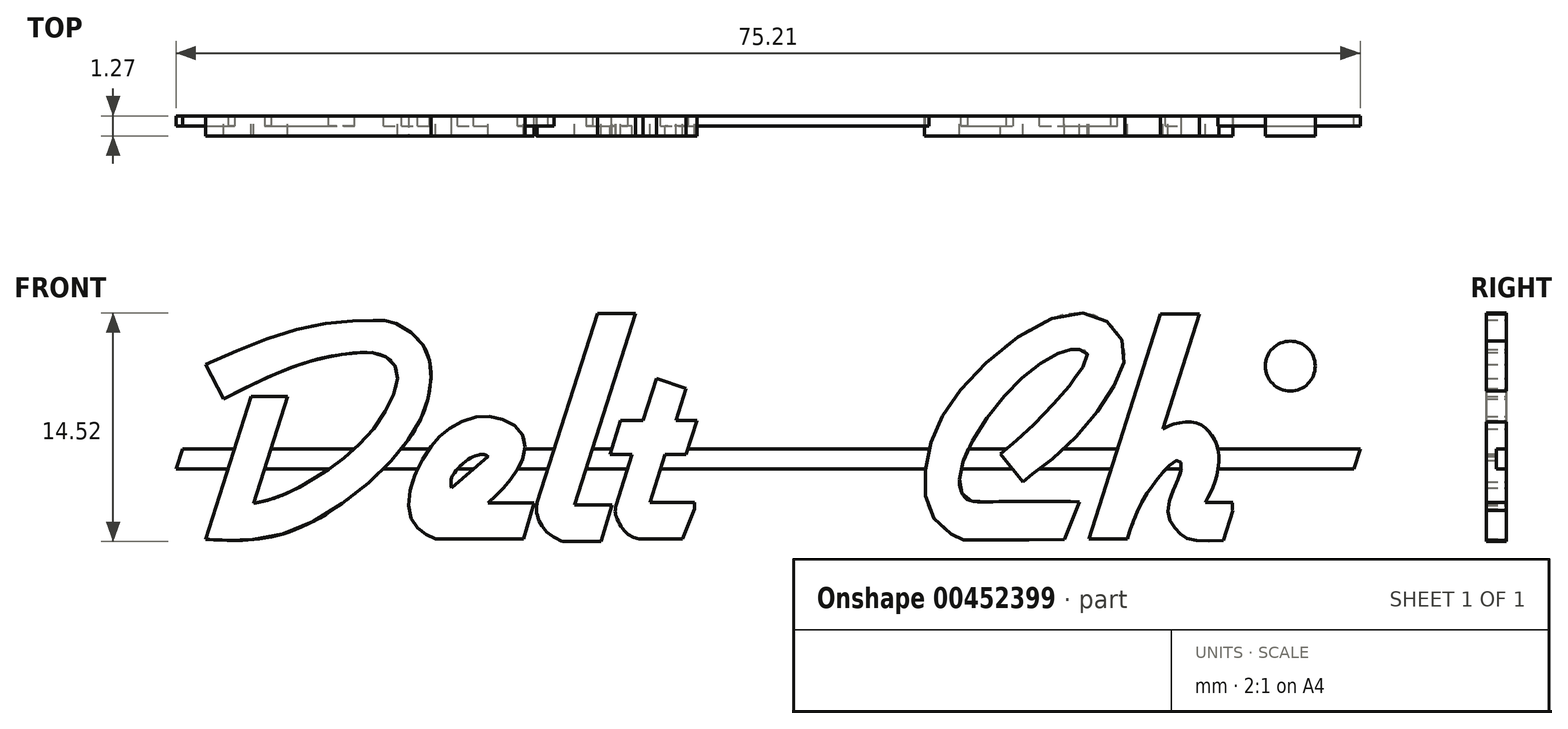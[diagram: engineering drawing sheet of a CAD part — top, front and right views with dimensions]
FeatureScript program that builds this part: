
annotation { "Feature Type Name" : "Feature", "Feature Type Description" : "" }
export const myFeature = defineFeature(function(context is Context, id is Id, definition is map)
    precondition{}
    {
        {
            var Q0;
            Q0=qCreatedBy(makeId("Front.planeOp"),FACE);
            var sketch = newSketch(context, id + "F0", { "sketchPlane" : qUnion([Q0])});
            skCircle(sketch, "E0", {"center": v(0, 0) * mm, "radius": 1.59 * mm});
            skCircle(sketch, "E1", {"center": v(82.55, 0) * mm, "radius": 1.59 * mm});
            skLineSegment(sketch, "E2", {"start": v(0, 0) * mm, "end": v(82.55, 0) * mm, "construction": true});
            skLineSegment(sketch, "E3", {"start": v(-6.39, 0) * mm, "end": v(88.9, 0) * mm, "construction": true});
            skEllipticalArc(sketch, "E4", {});
            skLineSegment(sketch, "E5", {"start": v(9.24, 2.96) * mm, "end": v(6.34, -6.11) * mm});
            skFitSpline(sketch, "E6", {"points": [v(6.34, -6.11) * mm, v(11.08, -5.82) * mm, v(17.7, -1.6) * mm, v(20.28, 2.23) * mm, v(20.6, 5.05) * mm, v(19.68, 6.78) * mm, v(17.97, 7.76) * mm, v(17.26, 7.8) * mm, v(13.33, 7.5) * mm, v(6.34, 4.98) * mm], "startDerivative": vector(26.1, -1) * mm, "endDerivative": vector(-45.15, -19.97) * mm});
            skLineSegment(sketch, "E7", {"start": v(9.24, 2.96) * mm, "end": v(11.56, 2.96) * mm});
            skLineSegment(sketch, "E8", {"start": v(11.56, 2.96) * mm, "end": v(9.38, -3.85) * mm});
            skFitSpline(sketch, "E9", {"points": [v(7.49, 2.8) * mm, v(9.85, 3.98) * mm, v(13.03, 5.22) * mm, v(15.23, 5.65) * mm, v(17.24, 5.7) * mm, v(18.43, 4.83) * mm, v(18.24, 2.96) * mm, v(16.2, 0) * mm, v(13.6, -2) * mm, v(11.58, -3.15) * mm, v(9.38, -3.85) * mm], "startDerivative": vector(21.38, 11.17) * mm, "endDerivative": vector(-26.6, -5.77) * mm});
            skLineSegment(sketch, "E10", {"start": v(6.34, 4.98) * mm, "end": v(7.49, 2.8) * mm});
            skLineSegment(sketch, "E11", {"start": v(24.28, -3.78) * mm, "end": v(27.21, -3.78) * mm});
            skLineSegment(sketch, "E12", {"start": v(27.21, -3.78) * mm, "end": v(26.52, -6.1) * mm});
            skLineSegment(sketch, "E13", {"start": v(26.52, -6.1) * mm, "end": v(20.93, -6.1) * mm});
            skFitSpline(sketch, "E14", {"points": [v(20.93, -6.1) * mm, v(20.03, -5.59) * mm, v(19.32, -4.54) * mm, v(19.49, -2.43) * mm, v(20.67, -0.21) * mm, v(21.8, 0.91) * mm, v(23.6, 1.67) * mm, v(25.31, 1.46) * mm, v(26.5, 0.48) * mm, v(26.5, -0.97) * mm, v(25.82, -2.13) * mm, v(25.09, -3.03) * mm, v(24.28, -3.78) * mm], "startDerivative": vector(-13.64, 6.23) * mm, "endDerivative": vector(-11.8, -10.28) * mm});
            skFitSpline(sketch, "E15", {"points": [v(21.97, -2.84) * mm, v(24.28, -0.85) * mm], "startDerivative": vector(2.31, 2) * mm, "endDerivative": vector(2.31, 2) * mm});
            skFitSpline(sketch, "E16", {"points": [v(21.97, -2.84) * mm, v(21.97, -2.19) * mm, v(22.96, -1.08) * mm, v(23.77, -0.73) * mm, v(24.28, -0.85) * mm], "startDerivative": vector(-0.63, 2.9) * mm, "endDerivative": vector(2.1, -1.88) * mm});
            skLineSegment(sketch, "E17", {"start": v(33.65, 8.22) * mm, "end": v(29.76, -3.94) * mm});
            skLineSegment(sketch, "E18", {"start": v(31.22, 8.22) * mm, "end": v(27.4, -3.75) * mm});
            skFitSpline(sketch, "E19", {"points": [v(27.4, -3.75) * mm, v(27.35, -4.28) * mm, v(27.67, -5.21) * mm, v(28.18, -5.78) * mm, v(28.68, -6.1) * mm, v(29.16, -6.25) * mm], "startDerivative": vector(-0.56, -2.65) * mm, "endDerivative": vector(2.82, 0.02) * mm});
            skLineSegment(sketch, "E20", {"start": v(29.16, -6.25) * mm, "end": v(31.45, -6.25) * mm});
            skLineSegment(sketch, "E21", {"start": v(31.45, -6.25) * mm, "end": v(32.16, -3.94) * mm});
            skLineSegment(sketch, "E22", {"start": v(32.16, -3.94) * mm, "end": v(29.76, -3.94) * mm});
            skLineSegment(sketch, "E23", {"start": v(33.65, 8.22) * mm, "end": v(31.22, 8.22) * mm});
            skLineSegment(sketch, "E24", {"start": v(32.7, 1.44) * mm, "end": v(34.12, 1.44) * mm});
            skLineSegment(sketch, "E25", {"start": v(37.55, 1.44) * mm, "end": v(36.86, -0.72) * mm});
            skLineSegment(sketch, "E26", {"start": v(36.86, -0.72) * mm, "end": v(35.52, -0.72) * mm});
            skLineSegment(sketch, "E27", {"start": v(32, -0.72) * mm, "end": v(32.7, 1.44) * mm});
            skLineSegment(sketch, "E28", {"start": v(34.97, 4.1) * mm, "end": v(34.12, 1.44) * mm});
            skFitSpline(sketch, "E29", {"points": [v(32.39, -3.97) * mm, v(32.39, -4.56) * mm, v(32.96, -5.6) * mm, v(33.66, -6.04) * mm, v(34.2, -6.08) * mm], "startDerivative": vector(-0.48, -3.27) * mm, "endDerivative": vector(2.58, 0) * mm});
            skLineSegment(sketch, "E30", {"start": v(34.2, -6.08) * mm, "end": v(36.64, -6.08) * mm});
            skLineSegment(sketch, "E31", {"start": v(36.64, -6.08) * mm, "end": v(37.38, -4.18) * mm});
            skLineSegment(sketch, "E32", {"start": v(37.4, -3.76) * mm, "end": v(34.55, -3.76) * mm});
            skLineSegment(sketch, "E33", {"start": v(34.55, -3.76) * mm, "end": v(35.52, -0.72) * mm});
            skLineSegment(sketch, "E34", {"start": v(36.86, 3.48) * mm, "end": v(34.97, 4.1) * mm});
            skLineSegment(sketch, "E35.trimOffspring", {"start": v(33.43, -0.72) * mm, "end": v(32.39, -3.97) * mm});
            skLineSegment(sketch, "E36.trimOffspring", {"start": v(36.21, 1.44) * mm, "end": v(36.86, 3.48) * mm});
            skLineSegment(sketch, "E37.trimOffspring", {"start": v(36.21, 1.44) * mm, "end": v(37.55, 1.44) * mm});
            skLineSegment(sketch, "E38.trimOffspring", {"start": v(33.43, -0.72) * mm, "end": v(32, -0.72) * mm});
            skFitSpline(sketch, "E39", {"points": [v(44.77, 1.43) * mm, v(41.69, 1) * mm, v(39.37, -0.26) * mm, v(37.87, -1.95) * mm, v(37.42, -3.48) * mm, v(37.55, -4.94) * mm, v(38.8, -6.04) * mm, v(40.81, -6.23) * mm, v(41.86, -5.63) * mm], "startDerivative": vector(-20.32, -1.3) * mm, "endDerivative": vector(9.3, 7.4) * mm});
            skFitSpline(sketch, "E40", {"points": [v(44.9, -0.76) * mm, v(44.25, -0.77) * mm, v(43.6, -0.86) * mm, v(41.6, -1.5) * mm, v(40.12, -2.55) * mm, v(39.68, -3.26) * mm, v(39.72, -3.97) * mm, v(40.65, -4) * mm, v(41.84, -2.63) * mm, v(42.1, -1.54) * mm], "startDerivative": vector(-16.55, 0.4) * mm, "endDerivative": vector(1.05, 9.2) * mm});
            skLineSegment(sketch, "E41", {"start": v(41.86, -5.63) * mm, "end": v(42.25, -5.63) * mm});
            skFitSpline(sketch, "E42", {"points": [v(42.25, -5.63) * mm, v(42.32, -5.88) * mm, v(42.53, -6.08) * mm, v(42.85, -6.13) * mm, v(42.86, -6.13) * mm], "startDerivative": vector(0.14, -0.88) * mm, "endDerivative": vector(0.11, 0.01) * mm});
            skLineSegment(sketch, "E43", {"start": v(42.85, -6.13) * mm, "end": v(45.2, -6.13) * mm});
            skLineSegment(sketch, "E44", {"start": v(45.2, -6.13) * mm, "end": v(46.1, -3.87) * mm});
            skLineSegment(sketch, "E45", {"start": v(46.1, -3.87) * mm, "end": v(43.54, -3.87) * mm});
            skFitSpline(sketch, "E46", {"points": [v(43.54, -3.87) * mm, v(43.87, -3.3) * mm, v(44.12, -2.21) * mm], "startDerivative": vector(0.7, 0.97) * mm, "endDerivative": vector(0.42, 3.16) * mm});
            skLineSegment(sketch, "E47", {"start": v(42.1, -1.54) * mm, "end": v(44.12, -2.21) * mm});
            skPoint(sketch, "E48.orphan", {"position": v(37.55, -3.76) * mm});
            skFitSpline(sketch, "E49", {"points": [v(56.83, -0.67) * mm, v(59.11, 1.35) * mm, v(61.4, 3.9) * mm, v(61.53, 4.1) * mm, v(62.26, 5.2) * mm, v(62.24, 5.84) * mm, v(61.58, 5.94) * mm, v(61.21, 5.94) * mm, v(59.63, 5.22) * mm, v(57, 2.92) * mm, v(54.62, -0.7) * mm, v(54.23, -2.62) * mm, v(54.65, -3.53) * mm, v(56.23, -3.72) * mm, v(61.83, -3.72) * mm], "startDerivative": vector(22.62, 18.51) * mm, "endDerivative": vector(50.2, -0.32) * mm});
            skFitSpline(sketch, "E50", {"points": [v(58.25, -2.47) * mm, v(58.7, -2.1) * mm, v(60.92, -0.33) * mm, v(63.78, 3.2) * mm, v(64.72, 5.72) * mm, v(63.66, 7.68) * mm, v(60.58, 8.1) * mm, v(55.2, 4.4) * mm, v(52.68, 0.8) * mm, v(52, -2.47) * mm, v(52.65, -4.84) * mm, v(54.17, -6.04) * mm, v(54.5, -6.14) * mm, v(54.66, -6.14) * mm, v(60.94, -6.13) * mm, v(60.95, -6.13) * mm], "startDerivative": vector(19.14, 15.4) * mm, "endDerivative": vector(-1.69, 2.05) * mm});
            skLineSegment(sketch, "E51", {"start": v(60.89, -6.13) * mm, "end": v(61.83, -3.72) * mm});
            skLineSegment(sketch, "E52", {"start": v(56.83, -0.67) * mm, "end": v(58.25, -2.47) * mm});
            skLineSegment(sketch, "E53", {"start": v(62.43, -6.08) * mm, "end": v(67, 8.2) * mm});
            skLineSegment(sketch, "E54", {"start": v(67, 8.2) * mm, "end": v(69.47, 8.2) * mm});
            skLineSegment(sketch, "E55", {"start": v(69.47, 8.2) * mm, "end": v(67.13, 0.89) * mm});
            skLineSegment(sketch, "E56", {"start": v(62.43, -6.08) * mm, "end": v(64.87, -6.08) * mm});
            skFitSpline(sketch, "E57", {"points": [v(64.87, -6.08) * mm, v(65.31, -4.84) * mm, v(65.94, -3.47) * mm, v(66.66, -2.46) * mm, v(67.33, -1.62) * mm, v(68.12, -1.1) * mm, v(68.32, -1.56) * mm, v(67.8, -3.01) * mm, v(67.5, -4.64) * mm, v(68.03, -5.54) * mm, v(68.78, -6.08) * mm, v(70.97, -6.18) * mm], "startDerivative": vector(3.34, 11.27) * mm, "endDerivative": vector(21.52, 0.39) * mm});
            skLineSegment(sketch, "E58", {"start": v(71.57, -4.3) * mm, "end": v(70.97, -6.18) * mm});
            skFitSpline(sketch, "E59", {"points": [v(67.13, 0.89) * mm, v(67.84, 1.2) * mm, v(69.29, 1.28) * mm, v(70.15, 0.6) * mm, v(70.66, -0.47) * mm, v(70.45, -2.45) * mm, v(69.83, -3.76) * mm], "startDerivative": vector(4.73, 2.62) * mm, "endDerivative": vector(-3.74, -6.76) * mm});
            skLineSegment(sketch, "E60", {"start": v(69.83, -3.76) * mm, "end": v(71.57, -3.76) * mm});
            skLineSegment(sketch, "E61", {"start": v(77.73, 8.35) * mm, "end": v(77.71, 8.29) * mm});
            skLineSegment(sketch, "E62", {"start": v(73.22, 1.43) * mm, "end": v(71.58, -3.72) * mm});
            skFitSpline(sketch, "E63", {"points": [v(71.58, -3.72) * mm, v(71.56, -4.21) * mm, v(71.88, -5.15) * mm, v(72.4, -5.72) * mm, v(72.9, -6.03) * mm, v(73.34, -6.22) * mm], "startDerivative": vector(-0.56, -2.65) * mm, "endDerivative": vector(2.82, 0.02) * mm});
            skLineSegment(sketch, "E64", {"start": v(73.34, -6.22) * mm, "end": v(75.37, -6.22) * mm});
            skLineSegment(sketch, "E65", {"start": v(75.37, -6.22) * mm, "end": v(76.08, -3.9) * mm});
            skLineSegment(sketch, "E66", {"start": v(76.08, -3.9) * mm, "end": v(73.81, -3.9) * mm});
            skLineSegment(sketch, "E67", {"start": v(73.22, 1.43) * mm, "end": v(75.52, 1.43) * mm});
            skLineSegment(sketch, "E68.trimOffspring", {"start": v(75.52, 1.43) * mm, "end": v(73.81, -3.9) * mm});
            skCircle(sketch, "E69", {"center": v(75.23, 4.9) * mm, "radius": 1.58 * mm});
            skPoint(sketch, "E69.first.point", {"position": v(75.46, 3.33) * mm});
            skPoint(sketch, "E69.second.point", {"position": v(73.83, 5.63) * mm});
            skPoint(sketch, "E69.third.point", {"position": v(76.25, 6.1) * mm});
            skLineSegment(sketch, "E70", {"start": v(44.77, 1.43) * mm, "end": v(44.9, -0.76) * mm});
            skLineSegment(sketch, "E71", {"start": v(-0.93, 8.33) * mm, "end": v(0.03, 6.5) * mm});
            skFitSpline(sketch, "E72", {"points": [v(16.41, -11.07) * mm, v(8.07, -9.5) * mm, v(0, -5.74) * mm, v(-2.2, -3.3) * mm, v(-3.2, -1.09) * mm, v(-3.35, 0) * mm], "startDerivative": vector(-32.01, 5.33) * mm, "endDerivative": vector(-0.5, 7.75) * mm});
            skFitSpline(sketch, "E73", {"points": [v(-5.42, 0) * mm, v(-4.76, -2.85) * mm, v(-2.05, -6.5) * mm, v(2.03, -9.2) * mm, v(7.58, -11.43) * mm, v(16.17, -13.37) * mm], "startDerivative": vector(-0.8, -17.85) * mm, "endDerivative": vector(30.13, -7.77) * mm});
            skLineSegment(sketch, "E74", {"start": v(-5.42, 0) * mm, "end": v(-3.35, 0) * mm});
            skEllipticalArc(sketch, "E75.trimOffspring", {});
            const initialGuessF0  = {"E4": [0.04125722514104046, 0, -1, 0, 0.047642774858959555, 0.012971381388337195, 1.0222549468718736, 5.758182635706344], "E75.trimOffspring": [0.04126686034929069, -2.0498317286381934e-05, -1, 0, 0.050181481787562376, 0.015419328761100942, 1.0471539651538773, 5.711128981700314]};
            skSetInitialGuess(sketch, initialGuessF0);
            skSolve(sketch);
        }
        {
            var Q0;
            Q0=makeQuery(id+"F0.imprint","IMPRINT",FACE,{"disambiguationData":[TD([[makeQuery(id+"F0.imprint","IMPRINT",EDGE,{"derivedFrom":sQuery(id+"F0.wireOp",EDGE,"E5")}),1.0]])]});
            var Q1;
            Q1=makeQuery(id+"F0.imprint","IMPRINT",FACE,{"disambiguationData":[TD([[makeQuery(id+"F0.imprint","IMPRINT",EDGE,{"derivedFrom":sQuery(id+"F0.wireOp",EDGE,"E11")}),-1.0]])]});
            var Q2;
            Q2=makeQuery(id+"F0.imprint","IMPRINT",FACE,{"disambiguationData":[TD([[makeQuery(id+"F0.imprint","IMPRINT",EDGE,{"derivedFrom":sQuery(id+"F0.wireOp",EDGE,"E17")}),-1.0]])]});
            var Q3;
            Q3=makeQuery(id+"F0.imprint","IMPRINT",FACE,{"disambiguationData":[TD([[makeQuery(id+"F0.imprint","IMPRINT",EDGE,{"derivedFrom":sQuery(id+"F0.wireOp",EDGE,"E24")}),-1.0]])]});
            var Q4;
            Q4=makeQuery(id+"F0.imprint","IMPRINT",FACE,{"disambiguationData":[TD([[makeQuery(id+"F0.imprint","IMPRINT",EDGE,{"derivedFrom":sQuery(id+"F0.wireOp",EDGE,"E49")}),-1.0]])]});
            var Q5;
            Q5=makeQuery(id+"F0.imprint","IMPRINT",FACE,{"disambiguationData":[TD([[makeQuery(id+"F0.imprint","IMPRINT",EDGE,{"derivedFrom":sQuery(id+"F0.wireOp",EDGE,"E53")}),-1.0]])]});
            var Q6;
            Q6=makeQuery(id+"F0.imprint","IMPRINT",FACE,{"disambiguationData":[TD([[makeQuery(id+"F0.imprint","IMPRINT",EDGE,{"derivedFrom":sQuery(id+"F0.wireOp",EDGE,"E69")}),1.0]])]});
            extrude(context, id + "F1", {"entities" : qUnion([Q0, Q1, Q2, Q3, Q4, Q5, Q6]), "depth" : 1.27 * mm});
        }
        {
            var Q0;
            Q0=makeQuery(id+"F1.opExtrude","SWEPT_BODY",BODY,{"disambiguationData":[OSD([sQuery(id+"F0.wireOp",EDGE,"E5"),sQuery(id+"F0.wireOp",EDGE,"E6"),sQuery(id+"F0.wireOp",EDGE,"E7"),sQuery(id+"F0.wireOp",EDGE,"E8"),sQuery(id+"F0.wireOp",EDGE,"E9"),sQuery(id+"F0.wireOp",EDGE,"E10")])]});
            var Q1;
            Q1=makeQuery(id+"F1.opExtrude","SWEPT_BODY",BODY,{"disambiguationData":[OSD([sQuery(id+"F0.wireOp",EDGE,"E11"),sQuery(id+"F0.wireOp",EDGE,"E12"),sQuery(id+"F0.wireOp",EDGE,"E13"),sQuery(id+"F0.wireOp",EDGE,"E14"),sQuery(id+"F0.wireOp",EDGE,"E15"),sQuery(id+"F0.wireOp",EDGE,"E16")])]});
            var Q2;
            Q2=makeQuery(id+"F1.opExtrude","SWEPT_BODY",BODY,{"disambiguationData":[OSD([sQuery(id+"F0.wireOp",EDGE,"E17"),sQuery(id+"F0.wireOp",EDGE,"E18"),sQuery(id+"F0.wireOp",EDGE,"E19"),sQuery(id+"F0.wireOp",EDGE,"E20"),sQuery(id+"F0.wireOp",EDGE,"E21"),sQuery(id+"F0.wireOp",EDGE,"E22"),sQuery(id+"F0.wireOp",EDGE,"E23")])]});
            var Q3;
            Q3=makeQuery(id+"F1.opExtrude","SWEPT_BODY",BODY,{"disambiguationData":[OSD([sQuery(id+"F0.wireOp",EDGE,"E24"),sQuery(id+"F0.wireOp",EDGE,"E25"),sQuery(id+"F0.wireOp",EDGE,"E26"),sQuery(id+"F0.wireOp",EDGE,"E27"),sQuery(id+"F0.wireOp",EDGE,"E28"),sQuery(id+"F0.wireOp",EDGE,"E29"),sQuery(id+"F0.wireOp",EDGE,"E30"),sQuery(id+"F0.wireOp",EDGE,"E31"),sQuery(id+"F0.wireOp",EDGE,"E32"),sQuery(id+"F0.wireOp",EDGE,"E33"),sQuery(id+"F0.wireOp",EDGE,"E34"),sQuery(id+"F0.wireOp",EDGE,"E35.trimOffspring"),sQuery(id+"F0.wireOp",EDGE,"E36.trimOffspring"),sQuery(id+"F0.wireOp",EDGE,"E37.trimOffspring"),sQuery(id+"F0.wireOp",EDGE,"E38.trimOffspring"),sQuery(id+"F0.wireOp",EDGE,"E39"),sQuery(id+"F0.wireOp",EDGE,"E40"),sQuery(id+"F0.wireOp",EDGE,"E41"),sQuery(id+"F0.wireOp",EDGE,"E42"),sQuery(id+"F0.wireOp",EDGE,"E43"),sQuery(id+"F0.wireOp",EDGE,"E44"),sQuery(id+"F0.wireOp",EDGE,"E45"),sQuery(id+"F0.wireOp",EDGE,"E46"),sQuery(id+"F0.wireOp",EDGE,"E47"),sQuery(id+"F0.wireOp",EDGE,"E39"),sQuery(id+"F0.wireOp",EDGE,"E70")])]});
            var Q4;
            Q4=makeQuery(id+"F1.opExtrude","SWEPT_BODY",BODY,{"disambiguationData":[OSD([sQuery(id+"F0.wireOp",EDGE,"E49"),sQuery(id+"F0.wireOp",EDGE,"E50"),sQuery(id+"F0.wireOp",EDGE,"E51"),sQuery(id+"F0.wireOp",EDGE,"E52")])]});
            var Q5;
            Q5=makeQuery(id+"F1.opExtrude","SWEPT_BODY",BODY,{"disambiguationData":[OSD([sQuery(id+"F0.wireOp",EDGE,"E53"),sQuery(id+"F0.wireOp",EDGE,"E54"),sQuery(id+"F0.wireOp",EDGE,"E55"),sQuery(id+"F0.wireOp",EDGE,"E56"),sQuery(id+"F0.wireOp",EDGE,"E57"),sQuery(id+"F0.wireOp",EDGE,"E58"),sQuery(id+"F0.wireOp",EDGE,"E59"),sQuery(id+"F0.wireOp",EDGE,"E60"),sQuery(id+"F0.wireOp",EDGE,"E62"),sQuery(id+"F0.wireOp",EDGE,"E63"),sQuery(id+"F0.wireOp",EDGE,"E64"),sQuery(id+"F0.wireOp",EDGE,"E65"),sQuery(id+"F0.wireOp",EDGE,"E66"),sQuery(id+"F0.wireOp",EDGE,"E67"),sQuery(id+"F0.wireOp",EDGE,"E68.trimOffspring"),sQuery(id+"F0.wireOp",EDGE,"E63")])]});
            var Q6;
            Q6=makeQuery(id+"F1.opExtrude","SWEPT_BODY",BODY,{"disambiguationData":[OSD([sQuery(id+"F0.wireOp",EDGE,"E69")])]});
            transform(context, id + "F2", {"entities" : qUnion([Q0, Q1, Q2, Q3, Q4, Q5, Q6]), "transformType" : TransformType.TRANSLATION_3D, "dx" : 0 * mm, "dy" : 0 * mm, "dz" : 1.02 * mm, "makeCopy" : false});
        }
        {
            var Q0;
            Q0=qCreatedBy(makeId("Front.planeOp"),FACE);
            var sketch = newSketch(context, id + "F3", { "sketchPlane" : qUnion([Q0])});
            skLineSegment(sketch, "E76", {"start": v(4.87, 0.64) * mm, "end": v(79.67, 0.64) * mm});
            skLineSegment(sketch, "E77", {"start": v(4.46, -0.64) * mm, "end": v(79.27, -0.64) * mm});
            skLineSegment(sketch, "E78", {"start": v(79.67, 0.64) * mm, "end": v(79.27, -0.64) * mm});
            skLineSegment(sketch, "E79", {"start": v(4.87, 0.64) * mm, "end": v(4.46, -0.63) * mm});
            skSolve(sketch);
        }
        {
            var Q0;
            Q0=makeQuery(id+"F3.imprint","IMPRINT",FACE,{"disambiguationData":[TD([[makeQuery(id+"F3.imprint","IMPRINT",EDGE,{"derivedFrom":sQuery(id+"F3.wireOp",EDGE,"E76")}),-1.0]])]});
            extrude(context, id + "F4", {"entities" : qUnion([Q0]), "operationType" : NewBodyOperationType.ADD, "depth" : 0.64 * mm});
        }
        {
            var Q0;
            {var subQ1=sQuery(id+"F0.wireOp",EDGE,"E71");Q0=makeQuery(id+"F0.imprint","IMPRINT",FACE,{"disambiguationData":[TD([[makeQuery(id+"F0.imprint","IMPRINT",EDGE,{"derivedFrom":subQ1}),1.0]])]});}
            extrude(context, id + "F5", {"entities" : qUnion([Q0]), "depth" : 0.64 * mm});
        }
        {
            var Q0;
            Q0=makeQuery(id+"F5.opExtrude","SWEPT_BODY",BODY,{"disambiguationData":[OSD([sQuery(id+"F0.wireOp",EDGE,"E4"),sQuery(id+"F0.wireOp",EDGE,"E71"),sQuery(id+"F0.wireOp",EDGE,"E72"),sQuery(id+"F0.wireOp",EDGE,"E73"),sQuery(id+"F0.wireOp",EDGE,"E74"),sQuery(id+"F0.wireOp",EDGE,"E75.trimOffspring")])]});
            transform(context, id + "F6", {"entities" : qUnion([Q0]), "transformType" : TransformType.TRANSLATION_3D, "dx" : 0 * mm, "dy" : 0 * mm, "dz" : 2.03 * mm, "makeCopy" : false});
        }
        {
            var Q0;
            Q0=makeQuery(id+"F5.opExtrude","SWEPT_BODY",BODY,{"disambiguationData":[OSD([sQuery(id+"F0.wireOp",EDGE,"E4"),sQuery(id+"F0.wireOp",EDGE,"E71"),sQuery(id+"F0.wireOp",EDGE,"E72"),sQuery(id+"F0.wireOp",EDGE,"E73"),sQuery(id+"F0.wireOp",EDGE,"E74"),sQuery(id+"F0.wireOp",EDGE,"E75.trimOffspring")])]});
            deleteBodies(context, id + "F7", {"entities" : qUnion([Q0])});
        }
    });
